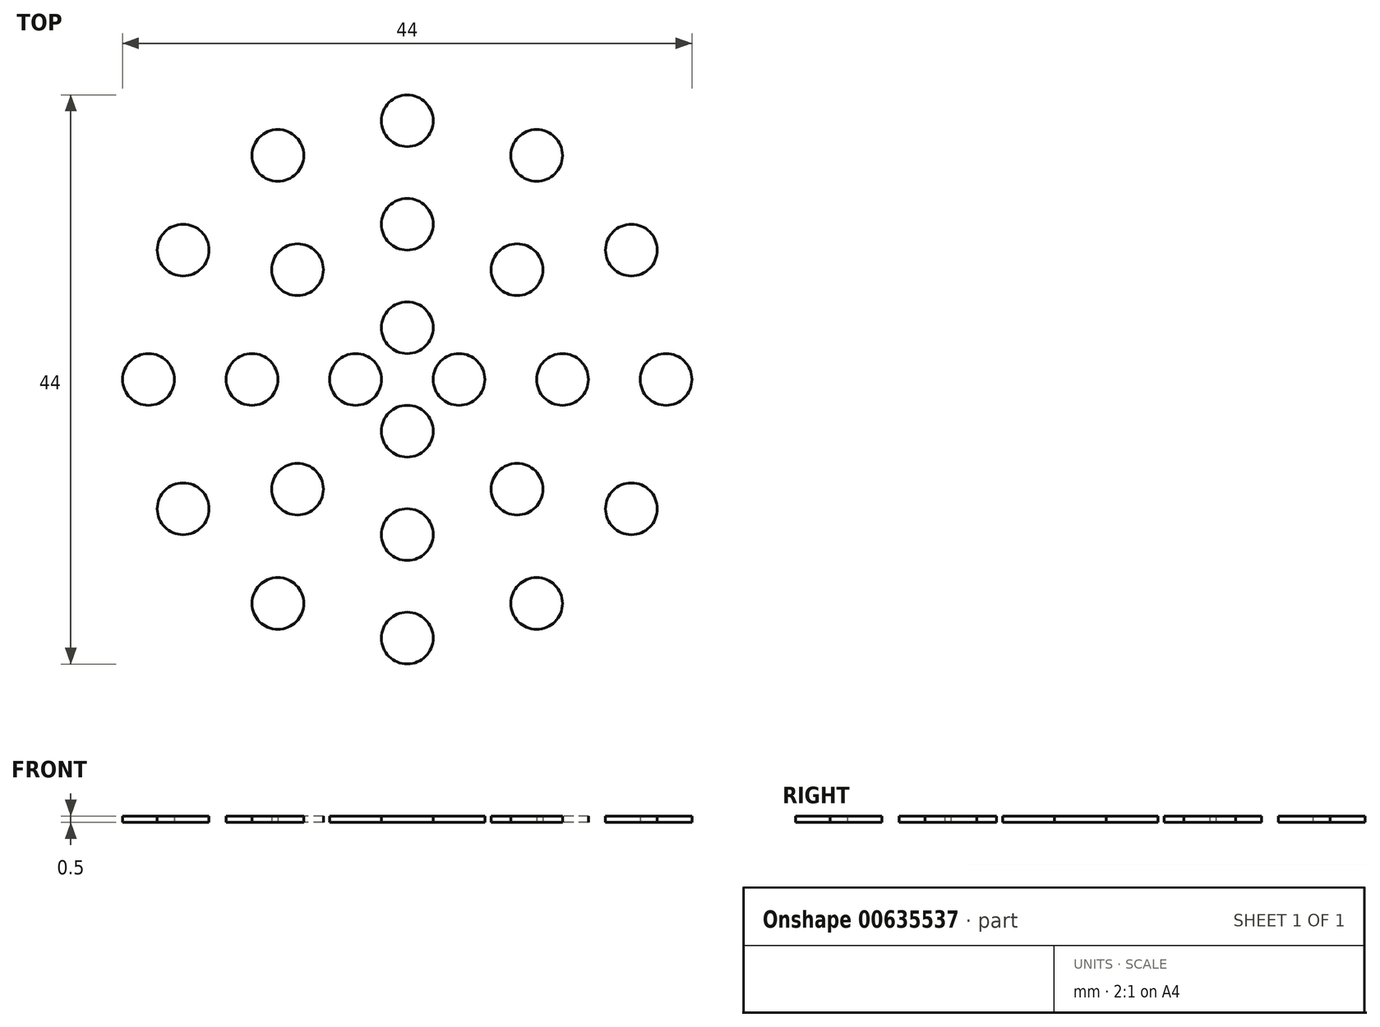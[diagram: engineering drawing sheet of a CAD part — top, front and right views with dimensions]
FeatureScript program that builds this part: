
annotation { "Feature Type Name" : "Feature", "Feature Type Description" : "" }
export const myFeature = defineFeature(function(context is Context, id is Id, definition is map)
    precondition{}
    {
        {
            var Q0;
            Q0=qCreatedBy(makeId("Top.planeOp"),FACE);
            var sketch = newSketch(context, id + "F0", { "sketchPlane" : qUnion([Q0])});
            skCircle(sketch, "E0", {"center": v(0, 0) * mm, "radius": 32.5 * mm});
            skLineSegment(sketch, "E1", {"start": v(0, 32.5) * mm, "end": v(0, -32.5) * mm, "construction": true});
            skLineSegment(sketch, "E2", {"start": v(-32.5, 0) * mm, "end": v(32.5, 0) * mm, "construction": true});
            skCircle(sketch, "E3", {"center": v(0, 0) * mm, "radius": 28.28 * mm});
            skLineSegment(sketch, "E4", {"start": v(0, 0) * mm, "end": v(-20, 20) * mm, "construction": true});
            skLineSegment(sketch, "E5", {"start": v(-20, 20) * mm, "end": v(-20, 0) * mm, "construction": true});
            skCircle(sketch, "E6", {"center": v(-20, 0) * mm, "radius": 2 * mm});
            skCircle(sketch, "E7.1.0", {"center": v(-17.32, -10) * mm, "radius": 2 * mm});
            skCircle(sketch, "E7.2.0", {"center": v(-10, -17.32) * mm, "radius": 2 * mm});
            skCircle(sketch, "E8.1.3.0", {"center": v(0, -20) * mm, "radius": 2 * mm});
            skCircle(sketch, "E8.1.4.0", {"center": v(10, -17.32) * mm, "radius": 2 * mm});
            skCircle(sketch, "E8.1.5.0", {"center": v(17.32, -10) * mm, "radius": 2 * mm});
            skCircle(sketch, "E8.1.6.0", {"center": v(20, 0) * mm, "radius": 2 * mm});
            skCircle(sketch, "E8.1.7.0", {"center": v(17.32, 10) * mm, "radius": 2 * mm});
            skCircle(sketch, "E8.1.8.0", {"center": v(10, 17.32) * mm, "radius": 2 * mm});
            skCircle(sketch, "E8.1.9.0", {"center": v(0, 20) * mm, "radius": 2 * mm});
            skCircle(sketch, "E9.1.10.0", {"center": v(-10, 17.32) * mm, "radius": 2 * mm});
            skCircle(sketch, "E9.1.11.0", {"center": v(-17.32, 10) * mm, "radius": 2 * mm});
            skCircle(sketch, "E10.1.0.0", {"center": v(-12, 0) * mm, "radius": 2 * mm});
            skLineSegment(sketch, "E10.direction1", {"start": v(-20, 0) * mm, "end": v(-12, 0) * mm, "construction": true});
            skCircle(sketch, "E11.1.0", {"center": v(-8.48, -8.48) * mm, "radius": 2 * mm});
            skCircle(sketch, "E11.2.0", {"center": v(0, -12) * mm, "radius": 2 * mm});
            skCircle(sketch, "E12.1.3.0", {"center": v(8.48, -8.48) * mm, "radius": 2 * mm});
            skCircle(sketch, "E12.1.4.0", {"center": v(12, 0) * mm, "radius": 2 * mm});
            skCircle(sketch, "E12.1.5.0", {"center": v(8.48, 8.48) * mm, "radius": 2 * mm});
            skCircle(sketch, "E13.1.0", {"center": v(0, -4) * mm, "radius": 2 * mm});
            skCircle(sketch, "E13.2.0", {"center": v(4, 0) * mm, "radius": 2 * mm});
            skCircle(sketch, "E14.1.3.0", {"center": v(0, 4) * mm, "radius": 2 * mm});
            skCircle(sketch, "E15.1.6.0", {"center": v(0, 12) * mm, "radius": 2 * mm});
            skCircle(sketch, "E15.1.7.0", {"center": v(-8.48, 8.48) * mm, "radius": 2 * mm});
            skCircle(sketch, "E16.0.2.0", {"center": v(-4, 0) * mm, "radius": 2 * mm});
            skSolve(sketch);
        }
        {
            var Q0;
            Q0=makeQuery(id+"F0.imprint","IMPRINT",FACE,{"disambiguationData":[TD([[makeQuery(id+"F0.imprint","IMPRINT",EDGE,{"derivedFrom":sQuery(id+"F0.wireOp",EDGE,"E7.1.0")}),1.0]])]});
            var Q1;
            Q1=makeQuery(id+"F0.imprint","IMPRINT",FACE,{"disambiguationData":[TD([[makeQuery(id+"F0.imprint","IMPRINT",EDGE,{"derivedFrom":sQuery(id+"F0.wireOp",EDGE,"E7.2.0")}),1.0]])]});
            var Q2;
            Q2=makeQuery(id+"F0.imprint","IMPRINT",FACE,{"disambiguationData":[TD([[makeQuery(id+"F0.imprint","IMPRINT",EDGE,{"derivedFrom":sQuery(id+"F0.wireOp",EDGE,"E8.1.3.0")}),1.0]])]});
            var Q3;
            Q3=makeQuery(id+"F0.imprint","IMPRINT",FACE,{"disambiguationData":[TD([[makeQuery(id+"F0.imprint","IMPRINT",EDGE,{"derivedFrom":sQuery(id+"F0.wireOp",EDGE,"E8.1.4.0")}),1.0]])]});
            var Q4;
            Q4=makeQuery(id+"F0.imprint","IMPRINT",FACE,{"disambiguationData":[TD([[makeQuery(id+"F0.imprint","IMPRINT",EDGE,{"derivedFrom":sQuery(id+"F0.wireOp",EDGE,"E12.1.3.0")}),1.0]])]});
            var Q5;
            Q5=makeQuery(id+"F0.imprint","IMPRINT",FACE,{"disambiguationData":[TD([[makeQuery(id+"F0.imprint","IMPRINT",EDGE,{"derivedFrom":sQuery(id+"F0.wireOp",EDGE,"E11.2.0")}),1.0]])]});
            var Q6;
            Q6=makeQuery(id+"F0.imprint","IMPRINT",FACE,{"disambiguationData":[TD([[makeQuery(id+"F0.imprint","IMPRINT",EDGE,{"derivedFrom":sQuery(id+"F0.wireOp",EDGE,"E11.1.0")}),1.0]])]});
            var Q7;
            Q7=makeQuery(id+"F0.imprint","IMPRINT",FACE,{"disambiguationData":[TD([[makeQuery(id+"F0.imprint","IMPRINT",EDGE,{"derivedFrom":sQuery(id+"F0.wireOp",EDGE,"E10.1.0.0")}),1.0]])]});
            var Q8;
            Q8=makeQuery(id+"F0.imprint","IMPRINT",FACE,{"disambiguationData":[TD([[makeQuery(id+"F0.imprint","IMPRINT",EDGE,{"derivedFrom":sQuery(id+"F0.wireOp",EDGE,"E6")}),1.0]])]});
            var Q9;
            Q9=makeQuery(id+"F0.imprint","IMPRINT",FACE,{"disambiguationData":[TD([[makeQuery(id+"F0.imprint","IMPRINT",EDGE,{"derivedFrom":sQuery(id+"F0.wireOp",EDGE,"E9.1.11.0")}),1.0]])]});
            var Q10;
            Q10=makeQuery(id+"F0.imprint","IMPRINT",FACE,{"disambiguationData":[TD([[makeQuery(id+"F0.imprint","IMPRINT",EDGE,{"derivedFrom":sQuery(id+"F0.wireOp",EDGE,"E15.1.7.0")}),1.0]])]});
            var Q11;
            Q11=makeQuery(id+"F0.imprint","IMPRINT",FACE,{"disambiguationData":[TD([[makeQuery(id+"F0.imprint","IMPRINT",EDGE,{"derivedFrom":sQuery(id+"F0.wireOp",EDGE,"E9.1.10.0")}),1.0]])]});
            var Q12;
            Q12=makeQuery(id+"F0.imprint","IMPRINT",FACE,{"disambiguationData":[TD([[makeQuery(id+"F0.imprint","IMPRINT",EDGE,{"derivedFrom":sQuery(id+"F0.wireOp",EDGE,"E15.1.6.0")}),1.0]])]});
            var Q13;
            Q13=makeQuery(id+"F0.imprint","IMPRINT",FACE,{"disambiguationData":[TD([[makeQuery(id+"F0.imprint","IMPRINT",EDGE,{"derivedFrom":sQuery(id+"F0.wireOp",EDGE,"E8.1.9.0")}),1.0]])]});
            var Q14;
            Q14=makeQuery(id+"F0.imprint","IMPRINT",FACE,{"disambiguationData":[TD([[makeQuery(id+"F0.imprint","IMPRINT",EDGE,{"derivedFrom":sQuery(id+"F0.wireOp",EDGE,"E8.1.8.0")}),1.0]])]});
            var Q15;
            Q15=makeQuery(id+"F0.imprint","IMPRINT",FACE,{"disambiguationData":[TD([[makeQuery(id+"F0.imprint","IMPRINT",EDGE,{"derivedFrom":sQuery(id+"F0.wireOp",EDGE,"E12.1.5.0")}),1.0]])]});
            var Q16;
            Q16=makeQuery(id+"F0.imprint","IMPRINT",FACE,{"disambiguationData":[TD([[makeQuery(id+"F0.imprint","IMPRINT",EDGE,{"derivedFrom":sQuery(id+"F0.wireOp",EDGE,"E8.1.7.0")}),1.0]])]});
            var Q17;
            Q17=makeQuery(id+"F0.imprint","IMPRINT",FACE,{"disambiguationData":[TD([[makeQuery(id+"F0.imprint","IMPRINT",EDGE,{"derivedFrom":sQuery(id+"F0.wireOp",EDGE,"E8.1.6.0")}),1.0]])]});
            var Q18;
            Q18=makeQuery(id+"F0.imprint","IMPRINT",FACE,{"disambiguationData":[TD([[makeQuery(id+"F0.imprint","IMPRINT",EDGE,{"derivedFrom":sQuery(id+"F0.wireOp",EDGE,"E8.1.5.0")}),1.0]])]});
            var Q19;
            Q19=makeQuery(id+"F0.imprint","IMPRINT",FACE,{"disambiguationData":[TD([[makeQuery(id+"F0.imprint","IMPRINT",EDGE,{"derivedFrom":sQuery(id+"F0.wireOp",EDGE,"E12.1.4.0")}),1.0]])]});
            var Q20;
            Q20=makeQuery(id+"F0.imprint","IMPRINT",FACE,{"disambiguationData":[TD([[makeQuery(id+"F0.imprint","IMPRINT",EDGE,{"derivedFrom":sQuery(id+"F0.wireOp",EDGE,"E13.2.0")}),1.0]])]});
            var Q21;
            Q21=makeQuery(id+"F0.imprint","IMPRINT",FACE,{"disambiguationData":[TD([[makeQuery(id+"F0.imprint","IMPRINT",EDGE,{"derivedFrom":sQuery(id+"F0.wireOp",EDGE,"E14.1.3.0")}),1.0]])]});
            var Q22;
            Q22=makeQuery(id+"F0.imprint","IMPRINT",FACE,{"disambiguationData":[TD([[makeQuery(id+"F0.imprint","IMPRINT",EDGE,{"derivedFrom":sQuery(id+"F0.wireOp",EDGE,"E13.1.0")}),1.0]])]});
            var Q23;
            Q23=makeQuery(id+"F0.imprint","IMPRINT",FACE,{"disambiguationData":[TD([[makeQuery(id+"F0.imprint","IMPRINT",EDGE,{"derivedFrom":sQuery(id+"F0.wireOp",EDGE,"E16.0.2.0")}),1.0]])]});
            extrude(context, id + "F1", {"entities" : qUnion([Q0, Q1, Q2, Q3, Q4, Q5, Q6, Q7, Q8, Q9, Q10, Q11, Q12, Q13, Q14, Q15, Q16, Q17, Q18, Q19, Q20, Q21, Q22, Q23]), "depth" : 0.5 * mm, "offsetDistance" : 25 * mm});
        }
    });
